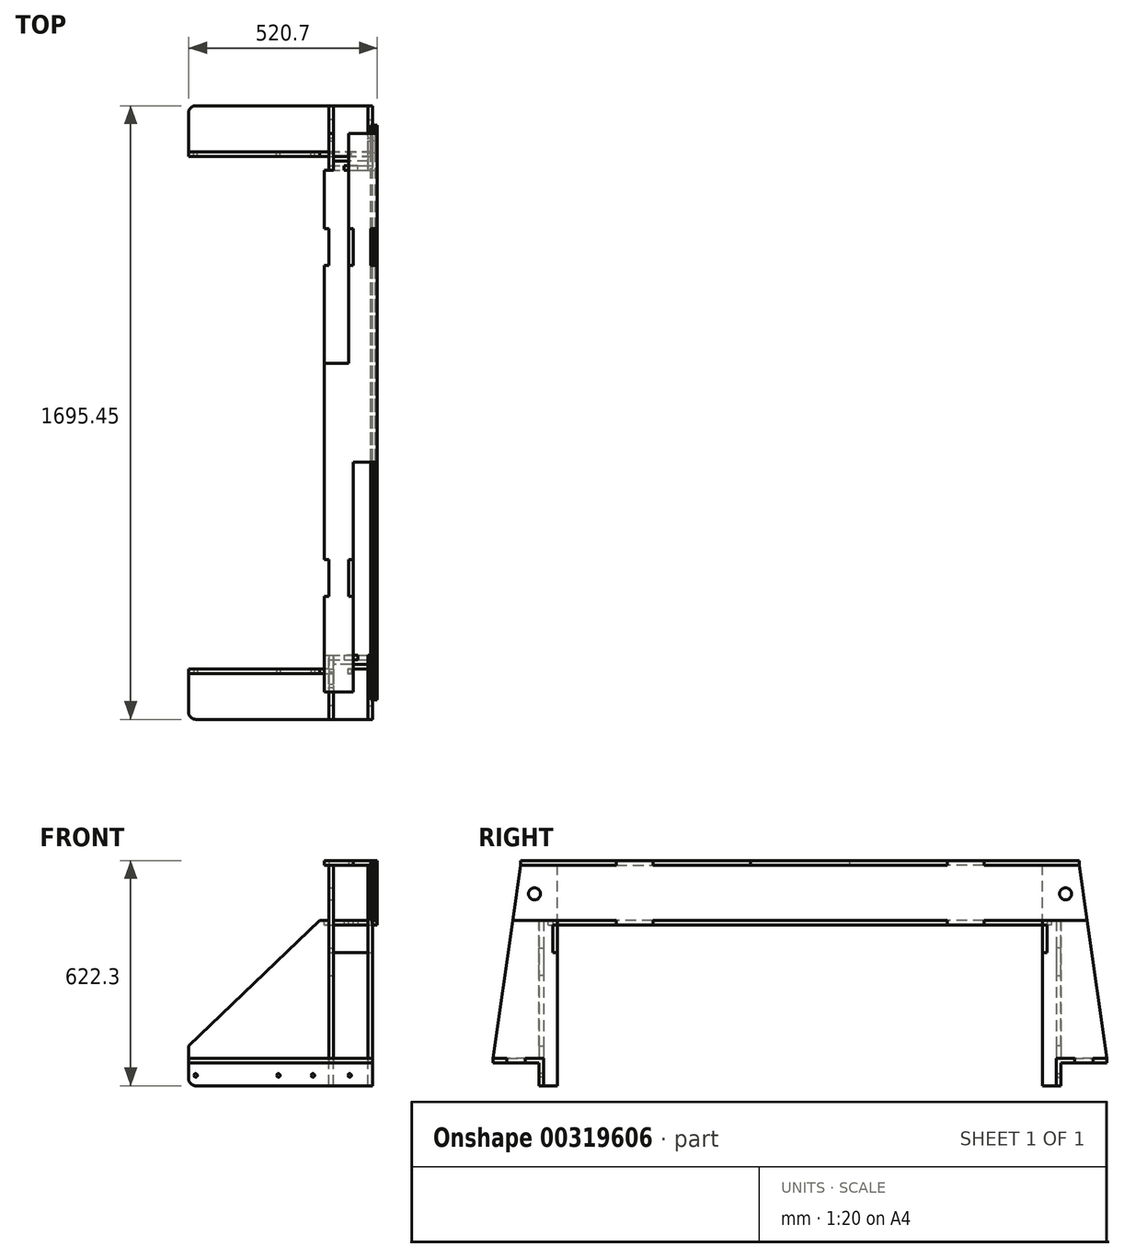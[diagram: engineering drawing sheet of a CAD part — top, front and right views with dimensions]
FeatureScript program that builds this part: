
annotation { "Feature Type Name" : "Feature", "Feature Type Description" : "" }
export const myFeature = defineFeature(function(context is Context, id is Id, definition is map)
    precondition{}
    {
        {
            var Q0;
            Q0=qCreatedBy(makeId("Top.planeOp"),FACE);
            var sketch = newSketch(context, id + "F0", { "sketchPlane" : qUnion([Q0])});
            skLineSegment(sketch, "E0", {"start": v(0, 0) * mm, "end": v(-508, 0) * mm});
            skLineSegment(sketch, "E1", {"start": v(-508, 0) * mm, "end": v(-508, 127) * mm});
            skLineSegment(sketch, "E2", {"start": v(-508, 127) * mm, "end": v(0, 127) * mm});
            skLineSegment(sketch, "E3", {"start": v(0, 127) * mm, "end": v(0, 0) * mm});
            skLineSegment(sketch, "E4.0", {"start": v(-12.7, 127) * mm, "end": v(-12.7, 0) * mm, "construction": true});
            skPoint(sketch, "E5", {"position": v(-12.7, 63.5) * mm});
            skPoint(sketch, "E6", {"position": v(-12.7, 38.1) * mm});
            skPoint(sketch, "E7", {"position": v(-12.7, 88.9) * mm});
            skLineSegment(sketch, "E8", {"start": v(-12.7, 88.9) * mm, "end": v(0, 88.9) * mm});
            skLineSegment(sketch, "E9", {"start": v(-12.7, 38.1) * mm, "end": v(0, 38.1) * mm});
            skLineSegment(sketch, "E10", {"start": v(-12.7, 88.9) * mm, "end": v(-12.7, 38.1) * mm});
            skLineSegment(sketch, "E11.0", {"start": v(-107.95, 127) * mm, "end": v(-107.95, 0) * mm, "construction": true});
            skLineSegment(sketch, "E12", {"start": v(-107.95, 88.9) * mm, "end": v(-107.95, 38.1) * mm, "construction": true});
            skLineSegment(sketch, "E13", {"start": v(-107.95, 88.9) * mm, "end": v(-120.65, 88.9) * mm});
            skLineSegment(sketch, "E14", {"start": v(-120.65, 88.9) * mm, "end": v(-120.65, 38.1) * mm});
            skLineSegment(sketch, "E15", {"start": v(-120.65, 38.1) * mm, "end": v(-107.95, 38.1) * mm});
            skLineSegment(sketch, "E16", {"start": v(-107.95, 88.9) * mm, "end": v(-107.95, 38.1) * mm});
            skSolve(sketch);
        }
        {
            var Q0;
            Q0=makeQuery(id+"F0.imprint","IMPRINT",FACE,{"disambiguationData":[TD([[makeQuery(id+"F0.imprint","IMPRINT",EDGE,{"derivedFrom":sQuery(id+"F0.wireOp",EDGE,"E0")}),-1.0]])]});
            extrude(context, id + "F1", {"entities" : qUnion([Q0]), "depth" : 12.7 * mm});
        }
        {
            var Q0;
            Q0=makeQuery(id+"F1.opExtrude","SWEPT_FACE",FACE,{"disambiguationData":[OSD([sQuery(id+"F0.wireOp",EDGE,"E0")])]});
            var sketch = newSketch(context, id + "F2", { "sketchPlane" : qUnion([Q0])});
            skLineSegment(sketch, "E17.0", {"start": v(0, 12.7) * mm, "end": v(-508, 12.7) * mm});
            skLineSegment(sketch, "E18", {"start": v(-508, 12.7) * mm, "end": v(-508, -63.5) * mm});
            skPoint(sketch, "E18.endSnap0", {"position": v(-508, 6.35) * mm});
            skLineSegment(sketch, "E19", {"start": v(-508, -63.5) * mm, "end": v(0, -63.5) * mm});
            skLineSegment(sketch, "E20", {"start": v(0, -63.5) * mm, "end": v(0, 12.7) * mm});
            skLineSegment(sketch, "E21.0", {"start": v(0, 0) * mm, "end": v(-508, 0) * mm, "construction": true});
            skPoint(sketch, "E22", {"position": v(-457.2, 0) * mm});
            skPoint(sketch, "E23", {"position": v(-381, 0) * mm});
            skPoint(sketch, "E24", {"position": v(-50.8, 0) * mm});
            skPoint(sketch, "E25", {"position": v(-127, 0) * mm});
            skLineSegment(sketch, "E26", {"start": v(-457.2, 0) * mm, "end": v(-381, 0) * mm});
            skLineSegment(sketch, "E27", {"start": v(-381, 0) * mm, "end": v(-381, 12.7) * mm});
            skLineSegment(sketch, "E28", {"start": v(-457.2, 0) * mm, "end": v(-457.2, 12.7) * mm});
            skLineSegment(sketch, "E29", {"start": v(-127, 0) * mm, "end": v(-50.8, 0) * mm});
            skLineSegment(sketch, "E30", {"start": v(-50.8, 0) * mm, "end": v(-50.8, 12.7) * mm});
            skLineSegment(sketch, "E31", {"start": v(-127, 0) * mm, "end": v(-127, 12.7) * mm});
            skLineSegment(sketch, "E32.0", {"start": v(0, -34.93) * mm, "end": v(-508, -34.93) * mm, "construction": true});
            skCircle(sketch, "E33", {"center": v(-488.95, -34.93) * mm, "radius": 4.76 * mm});
            skCircle(sketch, "E34", {"center": v(-260.35, -34.93) * mm, "radius": 4.76 * mm});
            skCircle(sketch, "E35", {"center": v(-165.1, -34.93) * mm, "radius": 4.76 * mm});
            skCircle(sketch, "E36", {"center": v(-63.5, -34.93) * mm, "radius": 4.76 * mm});
            skSolve(sketch);
        }
        {
            var Q0;
            {var subQ3=sQuery(id+"F2.wireOp",EDGE,"E19");Q0=makeQuery(id+"F2.imprint","IMPRINT",FACE,{"disambiguationData":[TD([[makeQuery(id+"F2.imprint","IMPRINT",EDGE,{"derivedFrom":subQ3}),1.0]])]});}
            var Q1;
            {var subQ3=sQuery(id+"F2.wireOp",EDGE,"E28");Q1=makeQuery(id+"F2.imprint","IMPRINT",FACE,{"disambiguationData":[TD([[makeQuery(id+"F2.imprint","IMPRINT",EDGE,{"derivedFrom":subQ3}),1.0]])]});}
            var Q2;
            {var subQ3=sQuery(id+"F2.wireOp",EDGE,"E27");Q2=makeQuery(id+"F2.imprint","IMPRINT",FACE,{"disambiguationData":[TD([[makeQuery(id+"F2.imprint","IMPRINT",EDGE,{"derivedFrom":subQ3}),-1.0]])]});}
            var Q3;
            {var subQ3=sQuery(id+"F2.wireOp",EDGE,"E30");Q3=makeQuery(id+"F2.imprint","IMPRINT",FACE,{"disambiguationData":[TD([[makeQuery(id+"F2.imprint","IMPRINT",EDGE,{"derivedFrom":subQ3}),-1.0]])]});}
            extrude(context, id + "F3", {"entities" : qUnion([Q0, Q1, Q2, Q3]), "depth" : 12.7 * mm});
        }
        {
            var Q0;
            Q0=makeQuery(id+"F2.imprint","IMPRINT",FACE,{"disambiguationData":[TD([[makeQuery(id+"F2.imprint","IMPRINT",EDGE,{"derivedFrom":sQuery(id+"F2.wireOp",EDGE,"E26")}),-1.0]])]});
            var Q1;
            Q1=makeQuery(id+"F2.imprint","IMPRINT",FACE,{"disambiguationData":[TD([[makeQuery(id+"F2.imprint","IMPRINT",EDGE,{"derivedFrom":sQuery(id+"F2.wireOp",EDGE,"E29")}),-1.0]])]});
            var Q2;
            Q2=makeQuery(id+"F3.opExtrude","CAP_FACE",FACE,{"disambiguationData":[OSD([sQuery(id+"F2.wireOp",EDGE,"E17.0"),sQuery(id+"F2.wireOp",EDGE,"E18"),sQuery(id+"F2.wireOp",EDGE,"E19"),sQuery(id+"F2.wireOp",EDGE,"E20"),sQuery(id+"F2.wireOp",EDGE,"E26"),sQuery(id+"F2.wireOp",EDGE,"E27"),sQuery(id+"F2.wireOp",EDGE,"E28"),sQuery(id+"F2.wireOp",EDGE,"E29"),sQuery(id+"F2.wireOp",EDGE,"E30"),sQuery(id+"F2.wireOp",EDGE,"E31")])],"isStart":false});
            extrude(context, id + "F4", {"entities" : qUnion([Q0, Q1]), "operationType" : NewBodyOperationType.ADD, "endBound" : BoundingType.UP_TO_SURFACE, "endBoundEntityFace" : qUnion([Q2]), "depth" : 25.4 * mm});
        }
        {
            var Q0;
            Q0=makeQuery(id+"F1.opExtrude","SWEPT_FACE",FACE,{"disambiguationData":[OSD([sQuery(id+"F0.wireOp",EDGE,"E3")])]});
            var sketch = newSketch(context, id + "F5", { "sketchPlane" : qUnion([Q0])});
            skLineSegment(sketch, "E37.0", {"start": v(-12.7, -63.5) * mm, "end": v(-12.7, 12.7) * mm});
            skLineSegment(sketch, "E38.0", {"start": v(127, 12.7) * mm, "end": v(88.9, 12.7) * mm});
            skLineSegment(sketch, "E39", {"start": v(-12.7, 12.7) * mm, "end": v(38.1, 12.7) * mm});
            skLineSegment(sketch, "E40", {"start": v(-12.7, -63.5) * mm, "end": v(-50.8, -63.5) * mm});
            skLineSegment(sketch, "E41", {"start": v(-50.8, -63.5) * mm, "end": v(-50.8, 546.1) * mm});
            skLineSegment(sketch, "E42", {"start": v(-50.8, 546.1) * mm, "end": v(50.8, 546.1) * mm});
            skLineSegment(sketch, "E43", {"start": v(50.8, 546.1) * mm, "end": v(127, 12.7) * mm});
            skCircle(sketch, "E44", {"center": v(12.7, 466.73) * mm, "radius": 16.7 * mm});
            skLineSegment(sketch, "E45", {"start": v(12.7, 466.73) * mm, "end": v(-50.8, 466.73) * mm});
            skLineSegment(sketch, "E46", {"start": v(12.7, 466.73) * mm, "end": v(12.7, 546.1) * mm});
            skLineSegment(sketch, "E47.0", {"start": v(88.9, 0) * mm, "end": v(38.1, 0) * mm});
            skLineSegment(sketch, "E48", {"start": v(88.9, 0) * mm, "end": v(88.9, 12.7) * mm});
            skLineSegment(sketch, "E49", {"start": v(38.1, 0) * mm, "end": v(38.1, 12.7) * mm});
            skPoint(sketch, "E50", {"position": v(-50.8, 381) * mm});
            skPoint(sketch, "E51", {"position": v(-50.8, 304.8) * mm});
            skLineSegment(sketch, "E52", {"start": v(-50.8, 381) * mm, "end": v(-38.1, 381) * mm});
            skLineSegment(sketch, "E53", {"start": v(-38.1, 381) * mm, "end": v(-38.1, 304.8) * mm});
            skLineSegment(sketch, "E54", {"start": v(-38.1, 304.8) * mm, "end": v(-50.8, 304.8) * mm});
            skSolve(sketch);
        }
        {
            var Q0;
            Q0=makeQuery(id+"F5.imprint","IMPRINT",FACE,{"disambiguationData":[TD([[makeQuery(id+"F5.imprint","IMPRINT",EDGE,{"derivedFrom":sQuery(id+"F5.wireOp",EDGE,"E37.0")}),1.0]])]});
            var Q1;
            {var subQ1=sQuery(id+"F5.wireOp",EDGE,"E41");var subQ7=sQuery(id+"F5.wireOp",EDGE,"E42");var subQ8=makeQuery(id+"F5.imprint","INTERSECT",VERTEX,{"derivedFrom":[subQ1,subQ7]});Q1=makeQuery(id+"F5.imprint","IMPRINT",FACE,{"disambiguationData":[TD([[makeQuery(id+"F5.imprint","IMPRINT",EDGE,{"disambiguationData":[TD([[subQ8,1.0]])],"derivedFrom":subQ1}),-1.0]])]});}
            extrude(context, id + "F6", {"entities" : qUnion([Q0, Q1]), "oppositeDirection" : true, "depth" : 12.7 * mm});
        }
        {
            assignVariable(context, id + "F7", {"name" : "BW", "anyValue" : 4.25});
        }
        {
            var Q0;
            Q0=makeQuery(id+"F1.opExtrude","SWEPT_FACE",FACE,{"disambiguationData":[OSD([sQuery(id+"F0.wireOp",EDGE,"E16")])]});
            cPlane(context, id + "F8", {"entities" : qUnion([Q0]), "cplaneType" : CPlaneType.OFFSET, "offset" : 0 * mm, "oppositeDirection" : true, "width" : 152.4 * mm, "height" : 152.4 * mm});
        }
        {
            var Q0;
            Q0=qCreatedBy(id+"F8.planeOp",FACE);
            var sketch = newSketch(context, id + "F9", { "sketchPlane" : qUnion([Q0])});
            skLineSegment(sketch, "E55.0", {"start": v(50.8, 546.1) * mm, "end": v(-50.8, 546.1) * mm});
            skLineSegment(sketch, "E56.0", {"start": v(-50.8, 546.1) * mm, "end": v(-127, 12.7) * mm});
            skLineSegment(sketch, "E57.0", {"start": v(50.8, -63.5) * mm, "end": v(50.8, 546.1) * mm});
            skLineSegment(sketch, "E58.0", {"start": v(12.7, -63.5) * mm, "end": v(50.8, -63.5) * mm});
            skLineSegment(sketch, "E59.0", {"start": v(12.7, -63.5) * mm, "end": v(12.7, 12.7) * mm});
            skLineSegment(sketch, "E60.0", {"start": v(12.7, 12.7) * mm, "end": v(-38.1, 12.7) * mm});
            skPoint(sketch, "E61.0", {"position": v(-38.1, 6.35) * mm});
            skLineSegment(sketch, "E62.0", {"start": v(-88.9, 0) * mm, "end": v(-38.1, 0) * mm});
            skPoint(sketch, "E63.0", {"position": v(-88.9, 6.35) * mm});
            skLineSegment(sketch, "E64.0", {"start": v(-127, 12.7) * mm, "end": v(-88.9, 12.7) * mm});
            skLineSegment(sketch, "E65.0", {"start": v(-88.9, 0) * mm, "end": v(-88.9, 12.7) * mm});
            skLineSegment(sketch, "E66.0", {"start": v(-38.1, 0) * mm, "end": v(-38.1, 12.7) * mm});
            skLineSegment(sketch, "E67", {"start": v(12.7, 12.7) * mm, "end": v(12.7, 546.1) * mm, "construction": true});
            skLineSegment(sketch, "E68.0", {"start": v(0, 12.7) * mm, "end": v(0, 546.1) * mm, "construction": true});
            skPoint(sketch, "E69", {"position": v(12.7, 241.3) * mm});
            skLineSegment(sketch, "E70", {"start": v(12.7, 241.3) * mm, "end": v(0, 241.3) * mm});
            skPoint(sketch, "E70.endSnap0", {"position": v(0, 279.4) * mm});
            skLineSegment(sketch, "E71", {"start": v(0, 241.3) * mm, "end": v(0, 317.5) * mm});
            skLineSegment(sketch, "E72", {"start": v(0, 317.5) * mm, "end": v(12.7, 317.5) * mm});
            skLineSegment(sketch, "E73", {"start": v(12.7, 317.5) * mm, "end": v(12.7, 241.3) * mm});
            skCircle(sketch, "E74.0", {"center": v(-12.7, 466.73) * mm, "radius": 16.7 * mm});
            skLineSegment(sketch, "E75.0", {"start": v(50.8, 381) * mm, "end": v(38.1, 381) * mm});
            skLineSegment(sketch, "E76.0", {"start": v(38.1, 381) * mm, "end": v(38.1, 304.8) * mm});
            skLineSegment(sketch, "E77.0", {"start": v(38.1, 304.8) * mm, "end": v(50.8, 304.8) * mm});
            skSolve(sketch);
        }
        {
            var Q0;
            Q0=makeQuery(id+"F9.imprint","IMPRINT",FACE,{"disambiguationData":[TD([[makeQuery(id+"F9.imprint","IMPRINT",EDGE,{"derivedFrom":sQuery(id+"F9.wireOp",EDGE,"E55.0")}),1.0]])]});
            extrude(context, id + "F10", {"entities" : qUnion([Q0]), "depth" : 12.7 * mm});
        }
        {
            var Q0;
            Q0=makeQuery(id+"F6.opExtrude","SWEPT_FACE",FACE,{"disambiguationData":[OSD([sQuery(id+"F5.wireOp",EDGE,"E53")])]});
            var sketch = newSketch(context, id + "F11", { "sketchPlane" : qUnion([Q0])});
            skLineSegment(sketch, "E78.0", {"start": v(0, 381) * mm, "end": v(0, 304.8) * mm});
            skLineSegment(sketch, "E79.0", {"start": v(-120.65, 381) * mm, "end": v(-120.65, 304.8) * mm});
            skLineSegment(sketch, "E80", {"start": v(-120.65, 381) * mm, "end": v(-79.38, 381) * mm});
            skLineSegment(sketch, "E81", {"start": v(-120.65, 304.8) * mm, "end": v(0, 304.8) * mm});
            skLineSegment(sketch, "E82", {"start": v(-60.32, 381) * mm, "end": v(-60.32, 393.7) * mm, "construction": true});
            skLineSegment(sketch, "E83", {"start": v(-60.32, 393.7) * mm, "end": v(-41.27, 393.7) * mm});
            skLineSegment(sketch, "E84", {"start": v(-41.27, 393.7) * mm, "end": v(-41.27, 381) * mm});
            skLineSegment(sketch, "E85.MirrorCS", {"start": v(-60.32, 393.7) * mm, "end": v(-79.38, 393.7) * mm});
            skLineSegment(sketch, "E86.MirrorCS", {"start": v(-79.38, 393.7) * mm, "end": v(-79.38, 381) * mm});
            skLineSegment(sketch, "E87.trimOffspring", {"start": v(-41.27, 381) * mm, "end": v(0, 381) * mm});
            skSolve(sketch);
        }
        {
            var Q0;
            {var subQ2=sQuery(id+"F11.wireOp",EDGE,"E79.0");Q0=makeQuery(id+"F11.imprint","IMPRINT",FACE,{"disambiguationData":[TD([[makeQuery(id+"F11.imprint","IMPRINT",EDGE,{"derivedFrom":subQ2}),1.0]])]});}
            var Q1;
            {var subQ0=sQuery(id+"F11.wireOp",EDGE,"E78.0");Q1=makeQuery(id+"F11.imprint","IMPRINT",FACE,{"disambiguationData":[TD([[makeQuery(id+"F11.imprint","IMPRINT",EDGE,{"derivedFrom":subQ0}),-1.0]])]});}
            extrude(context, id + "F12", {"entities" : qUnion([Q0, Q1]), "depth" : 12.7 * mm});
        }
        {
            var Q0;
            {var subQ0=sQuery(id+"F2.wireOp",EDGE,"E17.0");Q0=makeQuery(id+"F3.opExtrude","SWEPT_FACE",FACE,{"disambiguationData":[OSD([subQ0]),TDD([makeQuery(id+"F2.imprint","IMPRINT",EDGE,{"disambiguationData":[TD([[makeQuery(id+"F2.imprint","INTERSECT",VERTEX,{"derivedFrom":[subQ0,sQuery(id+"F2.wireOp",EDGE,"E27")]}),1.0]])],"derivedFrom":subQ0})])]});}
            var sketch = newSketch(context, id + "F13", { "sketchPlane" : qUnion([Q0])});
            skLineSegment(sketch, "E88.0", {"start": v(-120.65, -12.7) * mm, "end": v(-120.65, 38.1) * mm});
            skLineSegment(sketch, "E89.0", {"start": v(-508, -12.7) * mm, "end": v(-508, 0) * mm});
            skLineSegment(sketch, "E90", {"start": v(-508, -12.7) * mm, "end": v(-120.65, -12.7) * mm});
            skLineSegment(sketch, "E91", {"start": v(-508, 0) * mm, "end": v(-120.65, 0) * mm});
            skSolve(sketch);
        }
        {
            var Q0;
            Q0=makeQuery(id+"F13.imprint","IMPRINT",FACE,{"disambiguationData":[TD([[makeQuery(id+"F13.imprint","IMPRINT",EDGE,{"derivedFrom":sQuery(id+"F13.wireOp",EDGE,"c8208c28-5663-4249-825d-4aff4fe314d8.0")}),1.0]])]});
            var Q1;
            {var subQ1=sQuery(id+"F2.wireOp",EDGE,"E17.0");var subQ2=makeQuery(id+"F3.opExtrude","SWEPT_EDGE",EDGE,{"disambiguationData":[OSD([subQ1,sQuery(id+"F2.wireOp",EDGE,"E27")])]});Q1=makeQuery(id+"F13.imprint","IMPRINT",FACE,{"disambiguationData":[TD([[makeQuery(id+"F13.imprint","IMPRINT",EDGE,{"derivedFrom":subQ2}),-1.0]])]});}
            var Q2;
            {var subQ0=sQuery(id+"F13.wireOp",EDGE,"E89.0");Q2=makeQuery(id+"F13.imprint","IMPRINT",FACE,{"disambiguationData":[TD([[makeQuery(id+"F13.imprint","IMPRINT",EDGE,{"derivedFrom":subQ0}),-1.0]])]});}
            var Q3;
            {var subQ5=makeQuery(id+"F3.opExtrude","SWEPT_EDGE",EDGE,{"disambiguationData":[OSD([sQuery(id+"F2.wireOp",EDGE,"E17.0"),sQuery(id+"F2.wireOp",EDGE,"E31")])]});Q3=makeQuery(id+"F13.imprint","IMPRINT",FACE,{"disambiguationData":[TD([[makeQuery(id+"F13.imprint","IMPRINT",EDGE,{"derivedFrom":subQ5}),-1.0]])]});}
            extrude(context, id + "F14", {"entities" : qUnion([Q0, Q1, Q2, Q3]), "depth" : 381 * mm});
        }
        {
            var Q0;
            Q0=makeQuery(id+"F14.opExtrude","SWEPT_FACE",FACE,{"disambiguationData":[OSD([sQuery(id+"F13.wireOp",EDGE,"E90")])]});
            var sketch = newSketch(context, id + "F15", { "sketchPlane" : qUnion([Q0])});
            skLineSegment(sketch, "E92.0", {"start": v(-508, 12.7) * mm, "end": v(-120.65, 12.7) * mm});
            skLineSegment(sketch, "E93", {"start": v(-508, 12.7) * mm, "end": v(-508, 46.36) * mm});
            skLineSegment(sketch, "E94", {"start": v(-120.65, 393.7) * mm, "end": v(-146.05, 393.7) * mm});
            skLineSegment(sketch, "E95", {"start": v(-146.05, 393.7) * mm, "end": v(-508, 46.36) * mm});
            skSolve(sketch);
        }
        {
            var Q0;
            Q0=makeQuery(id+"F9.imprint","IMPRINT",FACE,{"disambiguationData":[TD([[makeQuery(id+"F9.imprint","IMPRINT",EDGE,{"derivedFrom":sQuery(id+"F9.wireOp",EDGE,"E70")}),-1.0]])]});
            extrude(context, id + "F16", {"entities" : qUnion([Q0]), "endBound" : BoundingType.UP_TO_NEXT, "depth" : 25.4 * mm});
        }
        {
            var Q0;
            {var subQ0=sQuery(id+"F15.wireOp",EDGE,"E95");Q0=makeQuery(id+"F15.imprint","IMPRINT",FACE,{"disambiguationData":[TD([[makeQuery(id+"F15.imprint","IMPRINT",EDGE,{"derivedFrom":subQ0}),-1.0]])]});}
            extrude(context, id + "F17", {"entities" : qUnion([Q0]), "operationType" : NewBodyOperationType.REMOVE, "oppositeDirection" : true, "depth" : 25.4 * mm});
        }
        {
            var Q0;
            Q0=makeQuery(id+"F5.imprint","IMPRINT",FACE,{"disambiguationData":[TD([[makeQuery(id+"F5.imprint","IMPRINT",EDGE,{"derivedFrom":sQuery(id+"F5.wireOp",EDGE,"E44")}),1.0]])]});
            extrude(context, id + "F18", {"entities" : qUnion([Q0]), "oppositeDirection" : true, "depth" : (getVariable(context, 'BW') + 1) * mm});
        }
        {
            var Q0;
            Q0=makeQuery(id+"F17.boolean.opBoolean","COPY",EDGE,{"derivedFrom":makeQuery(id+"F17.opExtrude","SWEPT_EDGE",EDGE,{"disambiguationData":[OSD([sQuery(id+"F13.wireOp",EDGE,"E89.0"),sQuery(id+"F13.wireOp",EDGE,"E90"),sQuery(id+"F15.wireOp",EDGE,"E93"),sQuery(id+"F15.wireOp",EDGE,"E95")])]})});
            var Q1;
            Q1=makeQuery(id+"F1.opExtrude","SWEPT_EDGE",EDGE,{"disambiguationData":[OSD([sQuery(id+"F0.wireOp",EDGE,"E1"),sQuery(id+"F0.wireOp",EDGE,"E2")])]});
            var Q2;
            Q2=makeQuery(id+"F3.opExtrude","SWEPT_EDGE",EDGE,{"disambiguationData":[OSD([sQuery(id+"F2.wireOp",EDGE,"E18"),sQuery(id+"F2.wireOp",EDGE,"E19")])]});
            var Q3;
            Q3=makeQuery(id+"F17.boolean.opBoolean","COPY",EDGE,{"derivedFrom":makeQuery(id+"F17.opExtrude","SWEPT_EDGE",EDGE,{"disambiguationData":[OSD([sQuery(id+"F13.wireOp",EDGE,"E90"),sQuery(id+"F15.wireOp",EDGE,"E94"),sQuery(id+"F15.wireOp",EDGE,"E95")])]})});
            fillet(context, id + "F19", {"entities" : qUnion([Q0, Q1, Q2, Q3]), "radius" : 19.05 * mm, "tangentPropagation" : true, "allowEdgeOverflow" : false});
        }
        {
            var Q0;
            Q0=qCreatedBy(makeId("Front.planeOp"),FACE);
            cPlane(context, id + "F20", {"entities" : qUnion([Q0]), "cplaneType" : CPlaneType.OFFSET, "offset" : 720.72 * mm, "width" : 152.4 * mm, "height" : 152.4 * mm});
        }
        {
            var Q0;
            Q0=makeQuery(id+"F1.opExtrude","SWEPT_BODY",BODY,{"disambiguationData":[OSD([sQuery(id+"F0.wireOp",EDGE,"E0"),sQuery(id+"F0.wireOp",EDGE,"E1"),sQuery(id+"F0.wireOp",EDGE,"E2"),sQuery(id+"F0.wireOp",EDGE,"E3"),sQuery(id+"F0.wireOp",EDGE,"E8"),sQuery(id+"F0.wireOp",EDGE,"E9"),sQuery(id+"F0.wireOp",EDGE,"E10"),sQuery(id+"F0.wireOp",EDGE,"E13"),sQuery(id+"F0.wireOp",EDGE,"E14"),sQuery(id+"F0.wireOp",EDGE,"E15"),sQuery(id+"F0.wireOp",EDGE,"E16")])]});
            var Q1;
            Q1=makeQuery(id+"F18.opExtrude","SWEPT_BODY",BODY,{"disambiguationData":[OSD([sQuery(id+"F5.wireOp",EDGE,"E44")])]});
            var Q2;
            Q2=makeQuery(id+"F10.opExtrude","SWEPT_BODY",BODY,{"disambiguationData":[OSD([sQuery(id+"F9.wireOp",EDGE,"E55.0"),sQuery(id+"F9.wireOp",EDGE,"E56.0"),sQuery(id+"F9.wireOp",EDGE,"E57.0"),sQuery(id+"F9.wireOp",EDGE,"E58.0"),sQuery(id+"F9.wireOp",EDGE,"E59.0"),sQuery(id+"F9.wireOp",EDGE,"E60.0"),sQuery(id+"F9.wireOp",EDGE,"E62.0"),sQuery(id+"F9.wireOp",EDGE,"E64.0"),sQuery(id+"F9.wireOp",EDGE,"E65.0"),sQuery(id+"F9.wireOp",EDGE,"E66.0")])]});
            var Q3;
            Q3=makeQuery(id+"F14.opExtrude","SWEPT_BODY",BODY,{"disambiguationData":[OSD([sQuery(id+"F13.wireOp",EDGE,"E88.0"),sQuery(id+"F13.wireOp",EDGE,"E89.0"),sQuery(id+"F13.wireOp",EDGE,"E90"),sQuery(id+"F13.wireOp",EDGE,"E91")])]});
            var Q4;
            Q4=makeQuery(id+"F6.opExtrude","SWEPT_BODY",BODY,{"disambiguationData":[OSD([sQuery(id+"F5.wireOp",EDGE,"E37.0"),sQuery(id+"F5.wireOp",EDGE,"E38.0"),sQuery(id+"F5.wireOp",EDGE,"E39"),sQuery(id+"F5.wireOp",EDGE,"E40"),sQuery(id+"F5.wireOp",EDGE,"E41"),sQuery(id+"F5.wireOp",EDGE,"E42"),sQuery(id+"F5.wireOp",EDGE,"E43"),sQuery(id+"F5.wireOp",EDGE,"E44"),sQuery(id+"F5.wireOp",EDGE,"E47.0"),sQuery(id+"F5.wireOp",EDGE,"E48"),sQuery(id+"F5.wireOp",EDGE,"E49")])]});
            var Q5;
            Q5=makeQuery(id+"F3.opExtrude","SWEPT_BODY",BODY,{"disambiguationData":[OSD([sQuery(id+"F2.wireOp",EDGE,"E17.0"),sQuery(id+"F2.wireOp",EDGE,"E18"),sQuery(id+"F2.wireOp",EDGE,"E19"),sQuery(id+"F2.wireOp",EDGE,"E20"),sQuery(id+"F2.wireOp",EDGE,"E26"),sQuery(id+"F2.wireOp",EDGE,"E27"),sQuery(id+"F2.wireOp",EDGE,"E28"),sQuery(id+"F2.wireOp",EDGE,"E29"),sQuery(id+"F2.wireOp",EDGE,"E30"),sQuery(id+"F2.wireOp",EDGE,"E31")])]});
            var Q6;
            Q6=makeQuery(id+"F12.opExtrude","SWEPT_BODY",BODY,{"disambiguationData":[OSD([sQuery(id+"F11.wireOp",EDGE,"E78.0"),sQuery(id+"F11.wireOp",EDGE,"E79.0"),sQuery(id+"F11.wireOp",EDGE,"E80"),sQuery(id+"F11.wireOp",EDGE,"E81"),sQuery(id+"F11.wireOp",EDGE,"E83"),sQuery(id+"F11.wireOp",EDGE,"E84"),sQuery(id+"F11.wireOp",EDGE,"E85.MirrorCS"),sQuery(id+"F11.wireOp",EDGE,"E86.MirrorCS"),sQuery(id+"F11.wireOp",EDGE,"E87.trimOffspring")])]});
            var Q7;
            Q7=qCreatedBy(id+"F20.planeOp",FACE);
            mirror(context, id + "F21", {"entities" : qUnion([Q0, Q1, Q2, Q3, Q4, Q5, Q6]), "mirrorPlane" : qUnion([Q7])});
        }
        {
            var Q0;
            Q0=makeQuery(id+"F21.opPattern","COPY",FACE,{"derivedFrom":makeQuery(id+"F6.opExtrude","CAP_FACE",FACE,{"disambiguationData":[OSD([sQuery(id+"F5.wireOp",EDGE,"E37.0"),sQuery(id+"F5.wireOp",EDGE,"E38.0"),sQuery(id+"F5.wireOp",EDGE,"E39"),sQuery(id+"F5.wireOp",EDGE,"E40"),sQuery(id+"F5.wireOp",EDGE,"E41"),sQuery(id+"F5.wireOp",EDGE,"E42"),sQuery(id+"F5.wireOp",EDGE,"E43"),sQuery(id+"F5.wireOp",EDGE,"E44")])],"isStart":true}),"instanceName":"1"});
            var sketch = newSketch(context, id + "F22", { "sketchPlane" : qUnion([Q0])});
            skLineSegment(sketch, "E96.0", {"start": v(-1492.25, 546.1) * mm, "end": v(-1514.02, 393.7) * mm});
            skLineSegment(sketch, "E97.0", {"start": v(50.8, 546.1) * mm, "end": v(72.57, 393.7) * mm});
            skCircle(sketch, "E98.0", {"center": v(12.7, 466.73) * mm, "radius": 16.7 * mm});
            skCircle(sketch, "E99.0", {"center": v(-1454.15, 466.73) * mm, "radius": 16.7 * mm});
            skLineSegment(sketch, "E100", {"start": v(-1492.25, 546.1) * mm, "end": v(50.8, 546.1) * mm});
            skLineSegment(sketch, "E101.0", {"start": v(-1514.02, 393.7) * mm, "end": v(72.57, 393.7) * mm});
            skPoint(sketch, "E102.orphan", {"position": v(-1568.45, 12.7) * mm});
            skPoint(sketch, "E103.orphan", {"position": v(127, 12.7) * mm});
            skLineSegment(sketch, "E104.0", {"start": v(-1228.73, 558.8) * mm, "end": v(-1127.13, 558.8) * mm});
            skLineSegment(sketch, "E105.0", {"start": v(-1228.73, 381) * mm, "end": v(-1127.13, 381) * mm});
            skLineSegment(sketch, "E106", {"start": v(-720.73, 546.1) * mm, "end": v(-720.73, 393.7) * mm, "construction": true});
            skLineSegment(sketch, "E107", {"start": v(-720.73, 469.9) * mm, "end": v(-314.33, 469.9) * mm, "construction": true});
            skLineSegment(sketch, "E108", {"start": v(-314.33, 469.9) * mm, "end": v(-720.73, 469.9) * mm, "construction": true});
            skLineSegment(sketch, "E109", {"start": v(-720.73, 469.9) * mm, "end": v(-1127.13, 469.9) * mm, "construction": true});
            skLineSegment(sketch, "E110", {"start": v(-314.33, 469.9) * mm, "end": v(-263.53, 469.9) * mm, "construction": true});
            skLineSegment(sketch, "E111", {"start": v(-263.53, 469.9) * mm, "end": v(-212.73, 469.9) * mm, "construction": true});
            skLineSegment(sketch, "E112", {"start": v(-1127.13, 469.9) * mm, "end": v(-1177.93, 469.9) * mm, "construction": true});
            skLineSegment(sketch, "E113", {"start": v(-1177.93, 469.9) * mm, "end": v(-1228.73, 469.9) * mm, "construction": true});
            skLineSegment(sketch, "E114", {"start": v(-212.73, 469.9) * mm, "end": v(-212.73, 558.8) * mm});
            skLineSegment(sketch, "E115", {"start": v(-314.33, 469.9) * mm, "end": v(-314.33, 558.8) * mm});
            skLineSegment(sketch, "E116", {"start": v(-314.33, 469.9) * mm, "end": v(-314.33, 381) * mm});
            skLineSegment(sketch, "E117", {"start": v(-212.73, 469.9) * mm, "end": v(-212.73, 381) * mm});
            skLineSegment(sketch, "E118", {"start": v(-1228.73, 469.9) * mm, "end": v(-1228.73, 558.8) * mm});
            skLineSegment(sketch, "E119", {"start": v(-1127.13, 469.9) * mm, "end": v(-1127.13, 558.8) * mm});
            skLineSegment(sketch, "E120", {"start": v(-1127.13, 469.9) * mm, "end": v(-1127.13, 381) * mm});
            skLineSegment(sketch, "E121", {"start": v(-1228.73, 469.9) * mm, "end": v(-1228.73, 381) * mm});
            skLineSegment(sketch, "E122.trimOffspring", {"start": v(-314.33, 558.8) * mm, "end": v(-212.73, 558.8) * mm});
            skLineSegment(sketch, "E123.trimOffspring", {"start": v(-314.33, 381) * mm, "end": v(-212.73, 381) * mm});
            skSolve(sketch);
        }
        {
            var Q0;
            {var subQ1=sQuery(id+"F22.wireOp",EDGE,"E97.0");Q0=makeQuery(id+"F22.imprint","IMPRINT",FACE,{"disambiguationData":[TD([[makeQuery(id+"F22.imprint","IMPRINT",EDGE,{"derivedFrom":subQ1}),-1.0]])]});}
            var Q1;
            {var subQ1=sQuery(id+"F22.wireOp",EDGE,"E96.0");Q1=makeQuery(id+"F22.imprint","IMPRINT",FACE,{"disambiguationData":[TD([[makeQuery(id+"F22.imprint","IMPRINT",EDGE,{"derivedFrom":subQ1}),1.0]])]});}
            var Q2;
            {var subQ1=sQuery(id+"F22.wireOp",EDGE,"E115");var subQ3=sQuery(id+"F22.wireOp",EDGE,"E100");var subQ4=makeQuery(id+"F22.imprint","INTERSECT",VERTEX,{"derivedFrom":[subQ3,subQ1]});Q2=makeQuery(id+"F22.imprint","IMPRINT",FACE,{"disambiguationData":[TD([[makeQuery(id+"F22.imprint","IMPRINT",EDGE,{"disambiguationData":[TD([[subQ4,-1.0]])],"derivedFrom":subQ3}),-1.0]])]});}
            var Q3;
            {var subQ5=sQuery(id+"F22.wireOp",EDGE,"E122.trimOffspring");Q3=makeQuery(id+"F22.imprint","IMPRINT",FACE,{"disambiguationData":[TD([[makeQuery(id+"F22.imprint","IMPRINT",EDGE,{"derivedFrom":subQ5}),-1.0]])]});}
            var Q4;
            {var subQ5=sQuery(id+"F22.wireOp",EDGE,"E123.trimOffspring");Q4=makeQuery(id+"F22.imprint","IMPRINT",FACE,{"disambiguationData":[TD([[makeQuery(id+"F22.imprint","IMPRINT",EDGE,{"derivedFrom":subQ5}),1.0]])]});}
            var Q5;
            {var subQ7=sQuery(id+"F22.wireOp",EDGE,"E100");var subQ9=sQuery(id+"F22.wireOp",EDGE,"E119");var subQ10=makeQuery(id+"F22.imprint","INTERSECT",VERTEX,{"derivedFrom":[subQ7,subQ9]});Q5=makeQuery(id+"F22.imprint","IMPRINT",FACE,{"disambiguationData":[TD([[makeQuery(id+"F22.imprint","IMPRINT",EDGE,{"disambiguationData":[TD([[subQ10,-1.0]])],"derivedFrom":subQ7}),-1.0]])]});}
            var Q6;
            {var subQ1=sQuery(id+"F22.wireOp",EDGE,"E118");var subQ3=sQuery(id+"F22.wireOp",EDGE,"E100");var subQ4=makeQuery(id+"F22.imprint","INTERSECT",VERTEX,{"derivedFrom":[subQ3,subQ1]});Q6=makeQuery(id+"F22.imprint","IMPRINT",FACE,{"disambiguationData":[TD([[makeQuery(id+"F22.imprint","IMPRINT",EDGE,{"disambiguationData":[TD([[subQ4,-1.0]])],"derivedFrom":subQ3}),-1.0]])]});}
            var Q7;
            {var subQ5=sQuery(id+"F22.wireOp",EDGE,"E104.0");Q7=makeQuery(id+"F22.imprint","IMPRINT",FACE,{"disambiguationData":[TD([[makeQuery(id+"F22.imprint","IMPRINT",EDGE,{"derivedFrom":subQ5}),-1.0]])]});}
            var Q8;
            {var subQ5=sQuery(id+"F22.wireOp",EDGE,"E105.0");Q8=makeQuery(id+"F22.imprint","IMPRINT",FACE,{"disambiguationData":[TD([[makeQuery(id+"F22.imprint","IMPRINT",EDGE,{"derivedFrom":subQ5}),1.0]])]});}
            var Q9;
            {var subQ1=sQuery(id+"F22.wireOp",EDGE,"E118");var subQ5=sQuery(id+"F22.wireOp",EDGE,"E100");var subQ9=makeQuery(id+"F22.imprint","INTERSECT",VERTEX,{"derivedFrom":[subQ5,subQ1]});Q9=makeQuery(id+"F22.imprint","IMPRINT",FACE,{"disambiguationData":[TD([[makeQuery(id+"F22.imprint","IMPRINT",EDGE,{"disambiguationData":[TD([[subQ9,1.0]])],"derivedFrom":subQ5}),-1.0]])]});}
            extrude(context, id + "F23", {"entities" : qUnion([Q0, Q1, Q2, Q3, Q4, Q5, Q6, Q7, Q8, Q9]), "depth" : 12.7 * mm});
        }
        {
            var Q0;
            Q0=makeQuery(id+"F23.opExtrude","SWEPT_BODY",BODY,{"disambiguationData":[OSD([sQuery(id+"F22.wireOp",EDGE,"E96.0"),sQuery(id+"F22.wireOp",EDGE,"E97.0"),sQuery(id+"F22.wireOp",EDGE,"E98.0"),sQuery(id+"F22.wireOp",EDGE,"E99.0"),sQuery(id+"F22.wireOp",EDGE,"E100"),sQuery(id+"F22.wireOp",EDGE,"E101.0")])]});
            transform(context, id + "F24", {"entities" : qUnion([Q0]), "transformType" : TransformType.TRANSLATION_3D, "dx" : (-getVariable(context, 'BW') - 1) * mm, "dy" : 0 * mm, "dz" : 0 * mm, "makeCopy" : true});
        }
        {
            var Q0;
            Q0=makeQuery(id+"F23.opExtrude","SWEPT_FACE",FACE,{"disambiguationData":[OSD([sQuery(id+"F22.wireOp",EDGE,"E100")])]});
            var sketch = newSketch(context, id + "F25", { "sketchPlane" : qUnion([Q0])});
            skLineSegment(sketch, "E124.0", {"start": v(-133.35, -1228.73) * mm, "end": v(-133.35, -1492.25) * mm});
            skLineSegment(sketch, "E125.0", {"start": v(12.7, -212.73) * mm, "end": v(12.7, 50.8) * mm});
            skLineSegment(sketch, "E126", {"start": v(-133.35, -1492.25) * mm, "end": v(-53.97, -1492.25) * mm});
            skLineSegment(sketch, "E127", {"start": v(12.7, 50.8) * mm, "end": v(-66.68, 50.8) * mm});
            skLineSegment(sketch, "E128", {"start": v(-53.97, -1492.25) * mm, "end": v(-53.98, -857.25) * mm});
            skLineSegment(sketch, "E129", {"start": v(-66.68, 50.8) * mm, "end": v(-66.67, -584.2) * mm});
            skLineSegment(sketch, "E130", {"start": v(-66.67, -584.2) * mm, "end": v(-133.35, -584.2) * mm});
            skLineSegment(sketch, "E131", {"start": v(-53.98, -857.25) * mm, "end": v(12.7, -857.25) * mm});
            skLineSegment(sketch, "E132", {"start": v(12.7, -857.25) * mm, "end": v(12.7, -314.33) * mm});
            skLineSegment(sketch, "E133", {"start": v(-133.35, -1127.13) * mm, "end": v(-133.35, -584.2) * mm});
            skLineSegment(sketch, "E134.0.1", {"start": v(-133.35, -1228.73) * mm, "end": v(-120.65, -1228.73) * mm});
            skLineSegment(sketch, "E134.0.2", {"start": v(-120.65, -1228.73) * mm, "end": v(-120.65, -1127.13) * mm});
            skLineSegment(sketch, "E134.0.3", {"start": v(-120.65, -1127.13) * mm, "end": v(-133.35, -1127.13) * mm});
            skLineSegment(sketch, "E135.0.0", {"start": v(0, -212.73) * mm, "end": v(0, -314.33) * mm});
            skLineSegment(sketch, "E135.0.1", {"start": v(0, -314.33) * mm, "end": v(12.7, -314.33) * mm});
            skLineSegment(sketch, "E135.0.3", {"start": v(12.7, -212.73) * mm, "end": v(0, -212.73) * mm});
            skLineSegment(sketch, "E136.0", {"start": v(-66.68, -1228.73) * mm, "end": v(-66.68, -1127.13) * mm});
            skLineSegment(sketch, "E137.0", {"start": v(-53.97, -212.73) * mm, "end": v(-53.97, -314.33) * mm});
            skLineSegment(sketch, "E138", {"start": v(-66.68, -1127.13) * mm, "end": v(-53.98, -1127.13) * mm});
            skLineSegment(sketch, "E139", {"start": v(-66.68, -1228.73) * mm, "end": v(-53.98, -1228.73) * mm});
            skLineSegment(sketch, "E140", {"start": v(-53.97, -314.33) * mm, "end": v(-66.67, -314.33) * mm});
            skLineSegment(sketch, "E141", {"start": v(-66.67, -314.33) * mm, "end": v(-64.72, -318.64) * mm});
            skLineSegment(sketch, "E142", {"start": v(-53.97, -212.73) * mm, "end": v(-66.67, -212.73) * mm});
            skLineSegment(sketch, "E143", {"start": v(-66.67, -212.73) * mm, "end": v(-62.67, -214.5) * mm});
            skSolve(sketch);
        }
        {
            var Q0;
            Q0=makeQuery(id+"F25.imprint","IMPRINT",FACE,{"disambiguationData":[TD([[makeQuery(id+"F25.imprint","IMPRINT",EDGE,{"derivedFrom":sQuery(id+"F25.wireOp",EDGE,"E124.0")}),1.0]])]});
            var Q1;
            {var subQ0=sQuery(id+"F25.wireOp",EDGE,"E132");Q1=makeQuery(id+"F25.imprint","IMPRINT",FACE,{"disambiguationData":[TD([[makeQuery(id+"F25.imprint","IMPRINT",EDGE,{"derivedFrom":subQ0}),1.0]])]});}
            var Q2;
            {var subQ0=sQuery(id+"F25.wireOp",EDGE,"E125.0");Q2=makeQuery(id+"F25.imprint","IMPRINT",FACE,{"disambiguationData":[TD([[makeQuery(id+"F25.imprint","IMPRINT",EDGE,{"derivedFrom":subQ0}),1.0]])]});}
            extrude(context, id + "F26", {"entities" : qUnion([Q0, Q1, Q2]), "depth" : 12.7 * mm});
        }
        {
            var Q0;
            Q0=makeQuery(id+"F23.opExtrude","SWEPT_FACE",FACE,{"disambiguationData":[OSD([sQuery(id+"F22.wireOp",EDGE,"E101.0")])]});
            var sketch = newSketch(context, id + "F27", { "sketchPlane" : qUnion([Q0])});
            skLineSegment(sketch, "E144.0", {"start": v(-120.65, 1390.65) * mm, "end": v(-107.95, 1390.65) * mm});
            skLineSegment(sketch, "E145.0", {"start": v(-12.7, 1390.65) * mm, "end": v(0, 1390.65) * mm});
            skLineSegment(sketch, "E146.0", {"start": v(-12.7, 50.8) * mm, "end": v(0, 50.8) * mm});
            skLineSegment(sketch, "E147.0", {"start": v(-120.65, 50.8) * mm, "end": v(-107.95, 50.8) * mm});
            skLineSegment(sketch, "E148", {"start": v(-120.65, 50.8) * mm, "end": v(-133.35, 50.8) * mm});
            skLineSegment(sketch, "E149", {"start": v(0, 50.8) * mm, "end": v(12.7, 50.8) * mm});
            skLineSegment(sketch, "E150", {"start": v(-120.65, 1390.65) * mm, "end": v(-133.35, 1390.65) * mm});
            skLineSegment(sketch, "E151", {"start": v(0, 1390.65) * mm, "end": v(12.7, 1390.65) * mm});
            skLineSegment(sketch, "E152.0.1", {"start": v(-133.35, 1127.13) * mm, "end": v(-120.65, 1127.13) * mm});
            skLineSegment(sketch, "E152.0.2", {"start": v(-120.65, 1127.13) * mm, "end": v(-120.65, 1228.73) * mm});
            skLineSegment(sketch, "E152.0.3", {"start": v(-120.65, 1228.73) * mm, "end": v(-133.35, 1228.73) * mm});
            skLineSegment(sketch, "E153.0.0", {"start": v(0, 1228.73) * mm, "end": v(0, 1127.13) * mm});
            skLineSegment(sketch, "E153.0.1", {"start": v(0, 1127.13) * mm, "end": v(12.7, 1127.13) * mm});
            skLineSegment(sketch, "E153.0.3", {"start": v(12.7, 1228.73) * mm, "end": v(0, 1228.73) * mm});
            skLineSegment(sketch, "E154.0.0", {"start": v(0, 314.33) * mm, "end": v(0, 212.73) * mm});
            skLineSegment(sketch, "E154.0.1", {"start": v(0, 212.73) * mm, "end": v(12.7, 212.73) * mm});
            skLineSegment(sketch, "E154.0.3", {"start": v(12.7, 314.33) * mm, "end": v(0, 314.33) * mm});
            skLineSegment(sketch, "E155.0.1", {"start": v(-133.35, 212.73) * mm, "end": v(-120.65, 212.73) * mm});
            skLineSegment(sketch, "E155.0.2", {"start": v(-120.65, 212.73) * mm, "end": v(-120.65, 314.33) * mm});
            skLineSegment(sketch, "E155.0.3", {"start": v(-120.65, 314.33) * mm, "end": v(-133.35, 314.33) * mm});
            skLineSegment(sketch, "E156", {"start": v(-133.35, 1127.13) * mm, "end": v(-133.35, 314.33) * mm});
            skLineSegment(sketch, "E157", {"start": v(12.7, 314.33) * mm, "end": v(12.7, 1127.13) * mm});
            skLineSegment(sketch, "E158", {"start": v(12.7, 212.73) * mm, "end": v(12.7, 50.8) * mm});
            skLineSegment(sketch, "E159", {"start": v(-133.35, 212.73) * mm, "end": v(-133.35, 50.8) * mm});
            skLineSegment(sketch, "E160", {"start": v(-133.35, 1390.65) * mm, "end": v(-133.35, 1228.73) * mm});
            skLineSegment(sketch, "E161", {"start": v(12.7, 1390.65) * mm, "end": v(12.7, 1228.73) * mm});
            skLineSegment(sketch, "E162.0", {"start": v(-53.97, 212.73) * mm, "end": v(-53.97, 314.33) * mm});
            skLineSegment(sketch, "E163.0", {"start": v(-53.97, 314.33) * mm, "end": v(-66.67, 314.33) * mm});
            skLineSegment(sketch, "E164.0", {"start": v(-53.97, 212.73) * mm, "end": v(-66.67, 212.73) * mm});
            skLineSegment(sketch, "E165.0", {"start": v(-66.68, 1228.73) * mm, "end": v(-66.68, 1127.13) * mm});
            skLineSegment(sketch, "E166.0", {"start": v(-66.68, 1127.13) * mm, "end": v(-53.98, 1127.13) * mm});
            skLineSegment(sketch, "E167.0", {"start": v(-66.68, 1228.73) * mm, "end": v(-53.98, 1228.73) * mm});
            skLineSegment(sketch, "E168", {"start": v(-53.97, 1228.73) * mm, "end": v(-53.97, 1127.13) * mm});
            skLineSegment(sketch, "E169", {"start": v(-66.68, 314.33) * mm, "end": v(-66.68, 212.73) * mm});
            skPoint(sketch, "E170.end.orphan", {"position": v(-12.7, 31.75) * mm});
            skPoint(sketch, "E171.end.orphan", {"position": v(-107.95, 31.75) * mm});
            skLineSegment(sketch, "E172", {"start": v(-12.7, 1390.65) * mm, "end": v(-107.95, 1390.65) * mm, "construction": true});
            skLineSegment(sketch, "E173", {"start": v(-12.7, 50.8) * mm, "end": v(-107.95, 50.8) * mm, "construction": true});
            skLineSegment(sketch, "E174.0", {"start": v(-12.7, 1416.05) * mm, "end": v(-107.95, 1416.05) * mm});
            skLineSegment(sketch, "E175", {"start": v(-12.7, 1416.05) * mm, "end": v(-12.7, 1390.65) * mm});
            skLineSegment(sketch, "E176", {"start": v(-107.95, 1416.05) * mm, "end": v(-107.95, 1390.65) * mm});
            skLineSegment(sketch, "E177.0", {"start": v(-12.7, 25.4) * mm, "end": v(-107.95, 25.4) * mm});
            skLineSegment(sketch, "E178", {"start": v(-12.7, 25.4) * mm, "end": v(-12.7, 50.8) * mm});
            skLineSegment(sketch, "E179", {"start": v(-107.95, 25.4) * mm, "end": v(-107.95, 50.8) * mm});
            skLineSegment(sketch, "E180.0.0", {"start": v(-79.38, 1403.35) * mm, "end": v(-41.27, 1403.35) * mm});
            skLineSegment(sketch, "E180.0.1", {"start": v(-41.27, 1403.35) * mm, "end": v(-41.27, 1390.65) * mm});
            skLineSegment(sketch, "E180.0.2", {"start": v(-41.27, 1390.65) * mm, "end": v(-79.38, 1390.65) * mm});
            skLineSegment(sketch, "E180.0.3", {"start": v(-79.38, 1390.65) * mm, "end": v(-79.38, 1403.35) * mm});
            skLineSegment(sketch, "E181.0.0", {"start": v(-41.27, 38.1) * mm, "end": v(-79.38, 38.1) * mm});
            skLineSegment(sketch, "E181.0.1", {"start": v(-79.38, 38.1) * mm, "end": v(-79.38, 50.8) * mm});
            skLineSegment(sketch, "E181.0.2", {"start": v(-79.38, 50.8) * mm, "end": v(-41.27, 50.8) * mm});
            skLineSegment(sketch, "E181.0.3", {"start": v(-41.27, 50.8) * mm, "end": v(-41.27, 38.1) * mm});
            skSolve(sketch);
        }
        {
            var Q0;
            Q0=makeQuery(id+"F27.imprint","IMPRINT",FACE,{"disambiguationData":[TD([[makeQuery(id+"F27.imprint","IMPRINT",EDGE,{"derivedFrom":sQuery(id+"F27.wireOp",EDGE,"E144.0")}),-1.0]])]});
            var Q1;
            Q1=makeQuery(id+"F27.imprint","IMPRINT",FACE,{"disambiguationData":[TD([[makeQuery(id+"F27.imprint","IMPRINT",EDGE,{"derivedFrom":sQuery(id+"F27.wireOp",EDGE,"E153.0.1")}),1.0]])]});
            var Q2;
            {var subQ0=sQuery(id+"F27.wireOp",EDGE,"E151");Q2=makeQuery(id+"F27.imprint","IMPRINT",FACE,{"disambiguationData":[TD([[makeQuery(id+"F27.imprint","IMPRINT",EDGE,{"derivedFrom":subQ0}),-1.0]])]});}
            var Q3;
            {var subQ0=sQuery(id+"F27.wireOp",EDGE,"E149");Q3=makeQuery(id+"F27.imprint","IMPRINT",FACE,{"disambiguationData":[TD([[makeQuery(id+"F27.imprint","IMPRINT",EDGE,{"derivedFrom":subQ0}),1.0]])]});}
            extrude(context, id + "F28", {"entities" : qUnion([Q0, Q1, Q2, Q3]), "depth" : 12.7 * mm});
        }
    });
